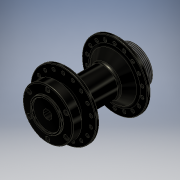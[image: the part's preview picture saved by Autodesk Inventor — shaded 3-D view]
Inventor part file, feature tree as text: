
AUTODESK INVENTOR PART (.ipt)
format: ipt  version: 2017 (Build 210142000, 142)  size: 483,840 bytes
history: native  units: mm
features: fillet x6, chamfer x5, sketch x5, extrude x4, pattern_circular x2, revolve x1, hole x1, direct_edit x1, thread x1, move_body x1
ambient origin geometry x8: Origin, YZ Plane, XZ Plane, XY Plane, X Axis, Y Axis, Z Axis, Center Point
bodies: Body1 (feature_tree)
feature tree (27):
  revolve  "Revolution1"  [1 undecoded]
  chamfer  "Chamfer1"  Distance=3.42mm
  fillet  "Fillet1"  Radius=6.0mm
  extrude  "Extrusion2"  Depth=26.0mm
  chamfer  "Chamfer2"  Distance=19.58mm
  pattern_circular  "Circular Pattern1"  [2 undecoded]
  extrude  "Extrusion3"  TaperAngle=90.0deg  [1 undecoded]
  chamfer  "Chamfer3"  Distance=10.0mm Angle=45.0deg
  pattern_circular  "Circular Pattern2"  [2 undecoded]
  extrude  "Extrusion4"  Depth=3.0mm
  fillet  "Fillet2"  Radius=5.0mm
  fillet  "Fillet3"  [1 undecoded]
  fillet  "Fillet4"  Radius=2.0mm
  fillet  "Fillet5"  Radius=180.0mm
  extrude  "Extrusion5"  Depth=3.0mm
  hole  "Hole1"  [1 undecoded]
  chamfer  "Chamfer5"  Distance=10.0mm
  chamfer  "Chamfer6"  Distance=2.0mm Angle=45.0deg
  direct_edit  "Direct Edit1"
  fillet  "Fillet6"  Radius=60.0mm
  thread  "Thread1"  [1 undecoded]
  sketch  "Sketch1"  dims[d3=15.0mm d4=49.8mm]
  sketch  "Sketch4"  dims[d5=34.0mm]
  sketch  "Sketch5"  dims[d6=34.0mm]
  sketch  "Sketch6"  dims[d7=21.5mm]
  sketch  "Sketch7"  dims[d8=3.42mm d9=3.42mm d10=6.0mm d11=26.0mm d12=19.58mm d13=17.5mm d14=90.0deg d15=10.0mm d16=2.0mm d17=45.0deg d18=4.0mm d19=2.7mm d21=5.0mm d22=0.0mm d23=0.0mm d24=0.5mm d25=2.0mm d26=45.0deg d27=180.0mm d28=360.0deg d30=4.01mm d31=4.0mm d32=10.0mm d33=0.0mm d34=0.5mm d35=2.0mm d36=45.0deg d37=60.0mm d38=360.0deg d40=38.0mm d41=29.0mm d42=17.0mm d43=0.0mm d47=6.0mm d48=2.0mm d49=1.0mm d50=0.6mm d51=32.8mm d52=29.0mm d53=2.0mm d54=0.0mm d55=10.0mm d56=10.0mm d57=9.02mm d58=6.0mm d59=4.0mm d60=2.0mm d61=90.0deg d62=8.0mm d63=20.594885mm d64=0.3mm d65=2.0mm d66=45.0deg d67=0.3mm d68=2.0mm d69=45.0deg d70=0.0mm d71=0.0mm d72=15.0mm d73=3.0mm d74=7.6mm d75=0.0mm]
  move_body  "Move1"
note: 9 required parameter values undecoded (feature->parameter linkage not recoverable at this tier; creation-order binding heuristic only, values carry confidence <= 0.55)